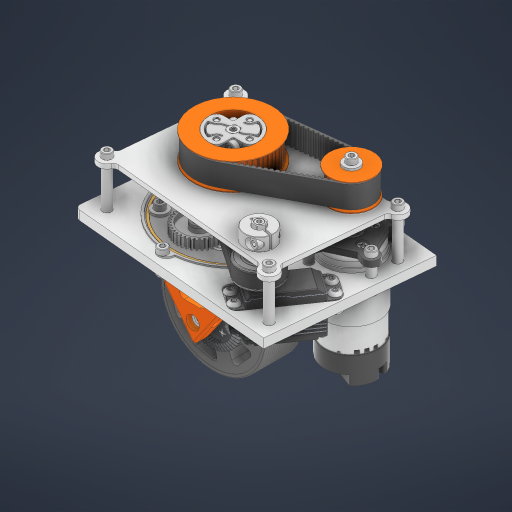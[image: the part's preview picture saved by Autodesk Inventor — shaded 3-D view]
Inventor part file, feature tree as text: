
AUTODESK INVENTOR PART (.ipt)
format: ipt  version: 2024.2 (Build 282272000, 272)  size: 59,893,760 bytes
history: native  units: in
note: dims shown in document units (in); Inventor stores cm internally (conversion verified against a paired STEP export)
features: other x130, plane x1
ambient origin geometry x8: Origin, YZ Plane, XZ Plane, XY Plane, X Axis, Y Axis, Z Axis, Center Point
bodies: Solid1 (feature_tree)
feature tree (131):
  other  "Pod.iam"
  other  "3ID3.5OD_Bearing.iam:1::outer race.ipt:1"
  other  "3ID3.5OD_Bearing.iam:1::shield.ipt:1"
  other  "3ID3.5OD_Bearing.iam:1::inner race.ipt:1"
  other  "AXON-ROBOTICS_PINION_BEVEL.ipt:1"
  other  "Modified_20Tooth_Pinion.ipt:1"
  other  "2807 Series Stainless Steel Shim (8mm ID x 11mm OD, 0.25mm Thickness) - 12 Pack.ipt:2"
  other  "Modified_36Tooth_Pinion.ipt:3"
  other  "AXON-ROBOTICS_HUB_BEVEL.ipt:1"
  other  "2801 Series Zinc-Plated Steel Washer (4mm ID x 11mm OD).ipt:1"
  other  "2802 Series Zinc-Plated Steel Button Head Screw (M4 x 0.7mm, 10mm Length) - 25 Pack.ipt:1"
  other  "Wheel_Base.ipt:1"
  other  "GGT.ipt:1"
  other  "2802 Series Zinc-Plated Steel Button Head Screw (M4 x 0.7mm, 10mm Length) - 25 Pack.ipt:2"
  other  "2801 Series Zinc Plated Steel Washer (4mm ID x 8mm OD) - 25 Pack.ipt:1"
  other  "1504 Series 32mm OD Pattern Spacer (2mm Length).ipt:1"
  other  "2807 Series Stainless Steel Shim (8mm ID x 11mm OD, 0.25mm Thickness) - 12 Pack.ipt:3"
  other  "2807 Series Stainless Steel Shim (8mm ID x 11mm OD, 0.25mm Thickness) - 12 Pack.ipt:4"
  other  "Rotation_Pulley.ipt:1"
  other  "1501 Series M4 x 0.7mm Standoff (6mm OD, 8mm Length) - 4 Pack.ipt:1"
  other  "1501 Series M4 x 0.7mm Standoff (6mm OD, 8mm Length) - 4 Pack.ipt:2"
  other  "1501 Series M4 x 0.7mm Standoff (6mm OD, 8mm Length) - 4 Pack.ipt:3"
  other  "1501 Series M4 x 0.7mm Standoff (6mm OD, 8mm Length) - 4 Pack.ipt:4"
  other  "Inner_Pod_Holder.ipt:1"
  other  "2801 Series Zinc-Plated Steel Washer (4mm ID x 11mm OD).ipt:2"
  other  "2801 Series Zinc-Plated Steel Washer (4mm ID x 11mm OD).ipt:3"
  other  "2801 Series Zinc-Plated Steel Washer (4mm ID x 11mm OD).ipt:4"
  other  "2801 Series Zinc-Plated Steel Washer (4mm ID x 11mm OD).ipt:5"
  other  "2801 Series Zinc-Plated Steel Washer (4mm ID x 11mm OD).ipt:6"
  other  "2801 Series Zinc-Plated Steel Washer (4mm ID x 11mm OD).ipt:7"
  other  "2801 Series Zinc-Plated Steel Washer (4mm ID x 11mm OD).ipt:8"
  other  "2801 Series Zinc-Plated Steel Washer (4mm ID x 11mm OD).ipt:9"
  other  "2800 Series Zinc-Plated Steel Socket Head Screw (M4 x 0.7mm, 14mm Length) - 25 Pack.ipt:1"
  other  "2800 Series Zinc-Plated Steel Socket Head Screw (M4 x 0.7mm, 14mm Length) - 25 Pack.ipt:2"
  other  "2800 Series Zinc-Plated Steel Socket Head Screw (M4 x 0.7mm, 14mm Length) - 25 Pack.ipt:3"
  other  "2800 Series Zinc-Plated Steel Socket Head Screw (M4 x 0.7mm, 14mm Length) - 25 Pack.ipt:4"
  other  "2812 Series Zinc-Plated Steel Nylon-Insert Locknut (M4 x 0.7mm, 7mm Hex) - 25 Pack.ipt:1"
  other  "2812 Series Zinc-Plated Steel Nylon-Insert Locknut (M4 x 0.7mm, 7mm Hex) - 25 Pack.ipt:2"
  other  "2812 Series Zinc-Plated Steel Nylon-Insert Locknut (M4 x 0.7mm, 7mm Hex) - 25 Pack.ipt:3"
  other  "2812 Series Zinc-Plated Steel Nylon-Insert Locknut (M4 x 0.7mm, 7mm Hex) - 25 Pack.ipt:4"
  other  "big_funny_washer.ipt:1"
  other  "2802 Series Zinc-Plated Steel Button Head Screw (M4 x 0.7mm, 10mm Length) - 25 Pack.ipt:3"
  other  "2802 Series Zinc-Plated Steel Button Head Screw (M4 x 0.7mm, 10mm Length) - 25 Pack.ipt:4"
  other  "2802 Series Zinc-Plated Steel Button Head Screw (M4 x 0.7mm, 10mm Length) - 25 Pack.ipt:5"
  other  "2802 Series Zinc-Plated Steel Button Head Screw (M4 x 0.7mm, 10mm Length) - 25 Pack.ipt:6"
  other  "2106 Series Stainless Steel REX Shaft (8mm Diameter, 40mm Length).iam:1::2106-4008-0400.ipt:1"
  other  "Wheel_Axle_Holder.ipt:1"
  other  "2801 Series Zinc Plated Steel Washer (4mm ID x 8mm OD) - 25 Pack.ipt:2"
  other  "2800 Series Zinc-Plated Steel Socket Head Screw (M4 x 0.7mm, 14mm Length) - 25 Pack.ipt:5"
  other  "2811 Series Zinc-Plated Steel Hex Nut (M4 x 0.7mm, 7mm Hex) - 25 Pack.ipt:1"
  other  "2811 Series Zinc-Plated Steel Hex Nut (M4 x 0.7mm, 7mm Hex) - 25 Pack.ipt:2"
  other  "2800 Series Zinc-Plated Steel Socket Head Screw (M4 x 0.7mm, 30mm Length) - 25 Pack.ipt:1"
  other  "2800 Series Zinc-Plated Steel Socket Head Screw (M4 x 0.7mm, 30mm Length) - 25 Pack.ipt:2"
  other  "HTD Pulley - 53 Tooth.ipt:1"
  other  "2807 Series Stainless Steel Shim (8mm ID x 11mm OD, 0.25mm Thickness) - 12 Pack.ipt:6"
  other  "28_Tooth.ipt:1"
  other  "2801 Series Zinc-Plated Steel Washer (4mm ID x 11mm OD).ipt:10"
  other  "2800 Series Zinc-Plated Steel Socket Head Screw (M4 x 0.7mm, 14mm Length) - 25 Pack.ipt:6"
  other  "Part Studio 1 - [LS] HTD3 belt 84 teeth.ipt:1"
  other  "1501 Series M4 x 0.7mm Standoff (6mm OD, 8mm Length) - 4 Pack.ipt:5"
  other  "Part Studio 1 - [LS] HTD5 belt 43 teeth.ipt:1"
  other  "Axon_MINI.iam:1::DDJ-STDLOW2-M2H-CNC.ipt:1"
  other  "Axon_MINI.iam:1::DDJ-STDLOW2-B-CNC.ipt:1"
  other  "Axon_MINI.iam:1::DDJ-STDLOW-LUOSI_3.ipt:1"
  other  "Axon_MINI.iam:1::DDJ-STDLOW-ZHOUCHENG.ipt:1"
  other  "Axon_MINI.iam:1::DDJ-STDLOW-LUOSI.ipt:1"
  other  "Axon_MINI.iam:1::DDJ-XT-22-3P.ipt:1"
  other  "Axon_MINI.iam:1::DDJ-STDLOW-LUOSI_1.ipt:1"
  other  "Axon_MINI.iam:1::DDJ-STDLOW-LUOSI_2.ipt:1"
  other  "Axon_MINI.iam:1::DDJ-STDLOW-GEAR6.ipt:1"
  other  "Lower_Plate.ipt:1"
  other  "1501 Series M4 x 0.7mm Standoff (6mm OD, 8mm Length) - 4 Pack.ipt:6"
  other  "2812 Series Zinc-Plated Steel Nylon-Insert Locknut (M4 x 0.7mm, 7mm Hex) - 25 Pack.ipt:5"
  other  "2802 Series Zinc-Plated Steel Button Head Screw (M4 x 0.7mm, 10mm Length) - 25 Pack.ipt:7"
  other  "2812 Series Zinc-Plated Steel Nylon-Insert Locknut (M4 x 0.7mm, 7mm Hex) - 25 Pack.ipt:6"
  other  "2802 Series Zinc-Plated Steel Button Head Screw (M4 x 0.7mm, 10mm Length) - 25 Pack.ipt:8"
  other  "2812 Series Zinc-Plated Steel Nylon-Insert Locknut (M4 x 0.7mm, 7mm Hex) - 25 Pack.ipt:7"
  other  "2802 Series Zinc-Plated Steel Button Head Screw (M4 x 0.7mm, 10mm Length) - 25 Pack.ipt:9"
  other  "2812 Series Zinc-Plated Steel Nylon-Insert Locknut (M4 x 0.7mm, 7mm Hex) - 25 Pack.ipt:8"
  other  "2802 Series Zinc-Plated Steel Button Head Screw (M4 x 0.7mm, 10mm Length) - 25 Pack.ipt:10"
  other  "2812 Series Zinc-Plated Steel Nylon-Insert Locknut (M4 x 0.7mm, 7mm Hex) - 25 Pack.ipt:9"
  other  "2800 Series Zinc-Plated Steel Socket Head Screw (M4 x 0.7mm, 12mm Length) - 25 Pack.ipt:1"
  other  "2812 Series Zinc-Plated Steel Nylon-Insert Locknut (M4 x 0.7mm, 7mm Hex) - 25 Pack.ipt:10"
  other  "2800 Series Zinc-Plated Steel Socket Head Screw (M4 x 0.7mm, 12mm Length) - 25 Pack.ipt:2"
  other  "2812 Series Zinc-Plated Steel Nylon-Insert Locknut (M4 x 0.7mm, 7mm Hex) - 25 Pack.ipt:11"
  other  "2800 Series Zinc-Plated Steel Socket Head Screw (M4 x 0.7mm, 12mm Length) - 25 Pack.ipt:3"
  other  "big_funny_washer.ipt:2"
  other  "2812 Series Zinc-Plated Steel Nylon-Insert Locknut (M4 x 0.7mm, 7mm Hex) - 25 Pack.ipt:13"
  other  "2800 Series Zinc-Plated Steel Socket Head Screw (M4 x 0.7mm, 12mm Length) - 25 Pack.ipt:5"
  other  "1501 Series M4 x 0.7mm Standoff (6mm OD, 8mm Length) - 4 Pack.ipt:7"
  other  "1501 Series M4 x 0.7mm Standoff (6mm OD, 8mm Length) - 4 Pack.ipt:8"
  other  "2800 Series Zinc-Plated Steel Socket Head Screw (M4 x 0.7mm, 14mm Length) - 25 Pack.ipt:7"
  other  "2800 Series Zinc-Plated Steel Socket Head Screw (M4 x 0.7mm, 14mm Length) - 25 Pack.ipt:8"
  other  "2800 Series Zinc-Plated Steel Socket Head Screw (M4 x 0.7mm, 14mm Length) - 25 Pack.ipt:9"
  other  "2800 Series Zinc-Plated Steel Socket Head Screw (M4 x 0.7mm, 14mm Length) - 25 Pack.ipt:10"
  other  "2800 Series Zinc-Plated Steel Socket Head Screw (M4 x 0.7mm, 7mm Length) - 25 Pack.ipt:1"
  other  "2800 Series Zinc-Plated Steel Socket Head Screw (M4 x 0.7mm, 7mm Length) - 25 Pack.ipt:2"
  other  "2800 Series Zinc-Plated Steel Socket Head Screw (M4 x 0.7mm, 7mm Length) - 25 Pack.ipt:3"
  other  "2800 Series Zinc-Plated Steel Socket Head Screw (M4 x 0.7mm, 7mm Length) - 25 Pack.ipt:4"
  other  "2800 Series Zinc-Plated Steel Socket Head Screw (M4 x 0.7mm, 7mm Length) - 25 Pack.ipt:5"
  other  "2800 Series Zinc-Plated Steel Socket Head Screw (M4 x 0.7mm, 7mm Length) - 25 Pack.ipt:6"
  other  "2800 Series Zinc-Plated Steel Socket Head Screw (M4 x 0.7mm, 7mm Length) - 25 Pack.ipt:7"
  other  "2800 Series Zinc-Plated Steel Socket Head Screw (M4 x 0.7mm, 7mm Length) - 25 Pack.ipt:8"
  other  "91698A729_Black-Oxide 18-8 Stainless Steel Phillips Flat Head Screws.ipt:1"
  other  "91698A729_Black-Oxide 18-8 Stainless Steel Phillips Flat Head Screws.ipt:2"
  other  "91698A729_Black-Oxide 18-8 Stainless Steel Phillips Flat Head Screws.ipt:3"
  other  "91698A729_Black-Oxide 18-8 Stainless Steel Phillips Flat Head Screws.ipt:4"
  other  "Wheel_Axle_Holder_MIR.ipt:1"
  other  "2800 Series Zinc-Plated Steel Socket Head Screw (M4 x 0.7mm, 14mm Length) - 25 Pack.ipt:11"
  other  "2811 Series Zinc-Plated Steel Hex Nut (M4 x 0.7mm, 7mm Hex) - 25 Pack.ipt:3"
  other  "2811 Series Zinc-Plated Steel Hex Nut (M4 x 0.7mm, 7mm Hex) - 25 Pack.ipt:4"
  other  "2800 Series Zinc-Plated Steel Socket Head Screw (M4 x 0.7mm, 30mm Length) - 25 Pack.ipt:3"
  other  "2800 Series Zinc-Plated Steel Socket Head Screw (M4 x 0.7mm, 30mm Length) - 25 Pack.ipt:4"
  other  "2807 Series Stainless Steel Shim (8mm ID x 11mm OD, 0.25mm Thickness) - 12 Pack.ipt:8"
  other  "Upper_Plate.ipt:1"
  other  "1501 Series M4 x 0.7mm Standoff (6mm OD, 28mm Length) - 4 Pack.ipt:1"
  other  "1501 Series M4 x 0.7mm Standoff (6mm OD, 28mm Length) - 4 Pack.ipt:2"
  other  "1501 Series M4 x 0.7mm Standoff (6mm OD, 28mm Length) - 4 Pack.ipt:3"
  other  "1501 Series M4 x 0.7mm Standoff (6mm OD, 28mm Length) - 4 Pack.ipt:4"
  other  "Power_Transmission_Spacer_One.ipt:1"
  other  "Servo_Spacer.ipt:1"
  other  "Power_Transmission_Space_Two.ipt:1"
  other  "2800 Series Zinc-Plated Steel Socket Head Screw (M4 x 0.7mm, 12mm Length) - 25 Pack.ipt:6"
  other  "2800 Series Zinc-Plated Steel Socket Head Screw (M4 x 0.7mm, 12mm Length) - 25 Pack.ipt:7"
  other  "2800 Series Zinc-Plated Steel Socket Head Screw (M4 x 0.7mm, 12mm Length) - 25 Pack.ipt:8"
  other  "2800 Series Zinc-Plated Steel Socket Head Screw (M4 x 0.7mm, 12mm Length) - 25 Pack.ipt:9"
  other  "2800 Series Zinc-Plated Steel Socket Head Screw (M4 x 0.7mm, 12mm Length) - 25 Pack.ipt:10"
  other  "2800 Series Zinc-Plated Steel Socket Head Screw (M4 x 0.7mm, 12mm Length) - 25 Pack.ipt:11"
  other  "2800 Series Zinc-Plated Steel Socket Head Screw (M4 x 0.7mm, 12mm Length) - 25 Pack.ipt:12"
  other  "2800 Series Zinc-Plated Steel Socket Head Screw (M4 x 0.7mm, 12mm Length) - 25 Pack.ipt:13"
  plane  "Work Plane2_1"
